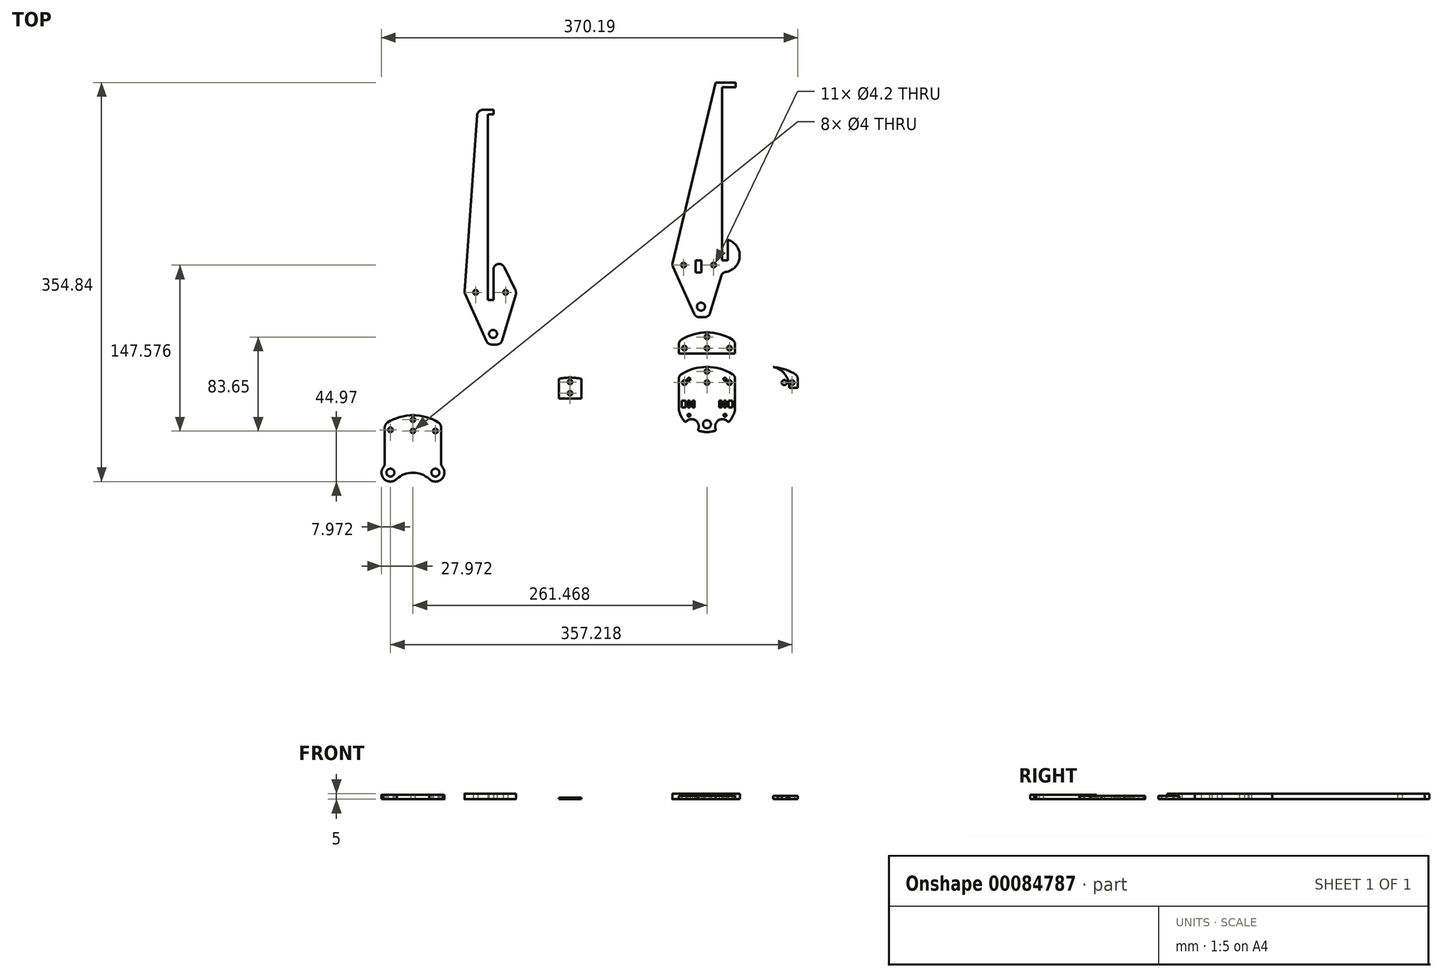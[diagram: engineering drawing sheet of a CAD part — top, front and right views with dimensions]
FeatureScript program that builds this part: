
annotation { "Feature Type Name" : "Feature", "Feature Type Description" : "" }
export const myFeature = defineFeature(function(context is Context, id is Id, definition is map)
    precondition{}
    {
        {
            var Q0;
            Q0=qCreatedBy(makeId("Top.planeOp"),FACE);
            var sketch = newSketch(context, id + "F0", { "sketchPlane" : qUnion([Q0])});
            skPoint(sketch, "E0.middle", {"position": v(0, 0) * mm});
            skLineSegment(sketch, "E1.top", {"start": v(-25, -10.03) * mm, "end": v(22.32, -10.03) * mm, "construction": true});
            skLineSegment(sketch, "E2.bottom", {"start": v(-20, 19) * mm, "end": v(20, 19) * mm, "construction": true});
            skCircle(sketch, "E3", {"center": v(-20, 19) * mm, "radius": 10 * mm, "construction": true});
            skCircle(sketch, "E4", {"center": v(0, -18) * mm, "radius": 10 * mm, "construction": true});
            skLineSegment(sketch, "E5.left", {"start": v(-25, 22.31) * mm, "end": v(-25, -5.6) * mm});
            skLineSegment(sketch, "E5.right", {"start": v(25, 22.31) * mm, "end": v(25, -5.6) * mm});
            skCircle(sketch, "E6", {"center": v(0, -18) * mm, "radius": 3.56 * mm});
            skCircle(sketch, "E7", {"center": v(-20, 19) * mm, "radius": 2.1 * mm});
            skCircle(sketch, "E8", {"center": v(20, 19) * mm, "radius": 2.1 * mm});
            skLineSegment(sketch, "E9", {"start": v(0, 0) * mm, "end": v(-25, 0) * mm, "construction": true});
            skLineSegment(sketch, "E10", {"start": v(0, 0) * mm, "end": v(0, 25) * mm, "construction": true});
            skLineSegment(sketch, "E11.bottom", {"start": v(-19, 3) * mm, "end": v(-22.5, 3) * mm});
            skLineSegment(sketch, "E11.top", {"start": v(-19, -3) * mm, "end": v(-22.5, -3) * mm});
            skLineSegment(sketch, "E11.left", {"start": v(-19, 3) * mm, "end": v(-19, -3) * mm});
            skLineSegment(sketch, "E11.right", {"start": v(-22.5, 3) * mm, "end": v(-22.5, -3) * mm});
            skPoint(sketch, "E11.middle", {"position": v(-20.75, 0) * mm});
            skLineSegment(sketch, "E12.bottom", {"start": v(-15, 3) * mm, "end": v(-17, 3) * mm});
            skLineSegment(sketch, "E12.top", {"start": v(-15, -3) * mm, "end": v(-17, -3) * mm});
            skLineSegment(sketch, "E12.left", {"start": v(-15, 3) * mm, "end": v(-15, -3) * mm});
            skLineSegment(sketch, "E12.right", {"start": v(-17, 3) * mm, "end": v(-17, -3) * mm});
            skPoint(sketch, "E12.middle", {"position": v(-16, 0) * mm});
            skLineSegment(sketch, "E13.bottom", {"start": v(-13, 3) * mm, "end": v(-11, 3) * mm});
            skLineSegment(sketch, "E13.top", {"start": v(-13, -3) * mm, "end": v(-11, -3) * mm});
            skLineSegment(sketch, "E13.left", {"start": v(-13, 3) * mm, "end": v(-13, -3) * mm});
            skLineSegment(sketch, "E13.right", {"start": v(-11, 3) * mm, "end": v(-11, -3) * mm});
            skPoint(sketch, "E13.middle", {"position": v(-12, 0) * mm});
            skLineSegment(sketch, "E14.MirrorCS", {"start": v(15, 3) * mm, "end": v(17, 3) * mm});
            skLineSegment(sketch, "E15.MirrorCS", {"start": v(13, -3) * mm, "end": v(11, -3) * mm});
            skLineSegment(sketch, "E16.MirrorCS", {"start": v(11, 3) * mm, "end": v(11, -3) * mm});
            skLineSegment(sketch, "E17.MirrorCS", {"start": v(13, 3) * mm, "end": v(11, 3) * mm});
            skPoint(sketch, "E18.MirrorP", {"position": v(16, 0) * mm});
            skLineSegment(sketch, "E19.MirrorCS", {"start": v(0, 0) * mm, "end": v(25, 0) * mm, "construction": true});
            skLineSegment(sketch, "E20.MirrorCS", {"start": v(22.5, 3) * mm, "end": v(22.5, -3) * mm});
            skLineSegment(sketch, "E21.MirrorCS", {"start": v(13, 3) * mm, "end": v(13, -3) * mm});
            skLineSegment(sketch, "E22.MirrorCS", {"start": v(15, 3) * mm, "end": v(15, -3) * mm});
            skLineSegment(sketch, "E23.MirrorCS", {"start": v(19, 3) * mm, "end": v(22.5, 3) * mm});
            skPoint(sketch, "E24.MirrorP", {"position": v(12, 0) * mm});
            skLineSegment(sketch, "E25.MirrorCS", {"start": v(19, 3) * mm, "end": v(19, -3) * mm});
            skLineSegment(sketch, "E26.MirrorCS", {"start": v(17, 3) * mm, "end": v(17, -3) * mm});
            skPoint(sketch, "E27.MirrorP", {"position": v(20.75, 0) * mm});
            skLineSegment(sketch, "E28.MirrorCS", {"start": v(19, -3) * mm, "end": v(22.5, -3) * mm});
            skLineSegment(sketch, "E29", {"start": v(15, -3) * mm, "end": v(17, -3) * mm});
            skCircle(sketch, "E30", {"center": v(0, 19) * mm, "radius": 2 * mm});
            skCircle(sketch, "E31", {"center": v(0, 29) * mm, "radius": 2 * mm});
            skLineSegment(sketch, "E32", {"start": v(0, 25) * mm, "end": v(0, 29) * mm, "construction": true});
            skArc(sketch, "E33", {"start": v(22.62, 26.57) * mm, "mid": v(0, 32.96) * mm, "end": v(-22.62, 26.57) * mm});
            skPoint(sketch, "E34", {"position": v(-20, 9) * mm});
            skPoint(sketch, "E35", {"position": v(-20, 10) * mm});
            skPoint(sketch, "E36.visualSharp", {"position": v(-25, -10.03) * mm});
            skPoint(sketch, "E37.visualSharp", {"position": v(-8, -24) * mm});
            skPoint(sketch, "E38", {"position": v(0, -8) * mm});
            skPoint(sketch, "E39", {"position": v(0, -10) * mm});
            skPoint(sketch, "E40.visualSharp", {"position": v(-25, 25) * mm});
            skArc(sketch, "E40.filletArc", {"start": v(-22.62, 26.57) * mm, "mid": v(-24.36, 24.75) * mm, "end": v(-25, 22.31) * mm});
            skPoint(sketch, "E41.visualSharp", {"position": v(25, 25) * mm});
            skArc(sketch, "E41.filletArc", {"start": v(25, 22.31) * mm, "mid": v(24.36, 24.75) * mm, "end": v(22.62, 26.57) * mm});
            skLineSegment(sketch, "E42.bottom", {"start": v(16, 22) * mm, "end": v(-16, 22) * mm, "construction": true});
            skLineSegment(sketch, "E42.top", {"start": v(16, -10) * mm, "end": v(-16, -10) * mm, "construction": true});
            skLineSegment(sketch, "E42.left", {"start": v(16, 22) * mm, "end": v(16, -10) * mm, "construction": true});
            skLineSegment(sketch, "E42.right", {"start": v(-16, 22) * mm, "end": v(-16, -10) * mm, "construction": true});
            skPoint(sketch, "E42.middle", {"position": v(0, 6) * mm});
            skCircle(sketch, "E43", {"center": v(-16, -10) * mm, "radius": 1.25 * mm});
            skCircle(sketch, "E44", {"center": v(16, -10) * mm, "radius": 1.25 * mm});
            skCircle(sketch, "E45", {"center": v(16, 22) * mm, "radius": 1.25 * mm});
            skCircle(sketch, "E46", {"center": v(-16, 22) * mm, "radius": 1.25 * mm});
            skPoint(sketch, "E47.orphan", {"position": v(25, -10.03) * mm});
            skPoint(sketch, "E48.orphan", {"position": v(8, -24) * mm});
            skLineSegment(sketch, "E49", {"start": v(-25, 14.31) * mm, "end": v(25, 14.31) * mm});
            skPoint(sketch, "E50.visualSharp", {"position": v(-21.13, -10.47) * mm});
            skArc(sketch, "E51", {"start": v(-25, -5.6) * mm, "mid": v(-23.01, -10.83) * mm, "end": v(-19.94, -15.51) * mm});
            skLineSegment(sketch, "E52", {"start": v(0, -18) * mm, "end": v(0, -24.93) * mm, "construction": true});
            skArc(sketch, "E53", {"start": v(0, -24.93) * mm, "mid": v(3.6, -24.67) * mm, "end": v(7.14, -23.92) * mm});
            skArc(sketch, "E54", {"start": v(-7.79, -22.56) * mm, "mid": v(-10.18, -14.59) * mm, "end": v(-18.44, -15.56) * mm});
            skArc(sketch, "E55.MirrorCS", {"start": v(7.79, -22.56) * mm, "mid": v(10.18, -14.59) * mm, "end": v(18.44, -15.56) * mm});
            skArc(sketch, "E56.trimOffspring", {"start": v(-7.14, -23.92) * mm, "mid": v(-3.6, -24.67) * mm, "end": v(0, -24.93) * mm});
            skArc(sketch, "E57.trimOffspring", {"start": v(19.94, -15.51) * mm, "mid": v(23.01, -10.83) * mm, "end": v(25, -5.6) * mm});
            skPoint(sketch, "E58.visualSharp", {"position": v(-19.14, -16.44) * mm});
            skArc(sketch, "E58.filletArc", {"start": v(-19.94, -15.51) * mm, "mid": v(-19.2, -15.88) * mm, "end": v(-18.44, -15.56) * mm});
            skPoint(sketch, "E59.visualSharp", {"position": v(-8.32, -23.55) * mm});
            skArc(sketch, "E59.filletArc", {"start": v(-7.79, -22.56) * mm, "mid": v(-7.77, -23.38) * mm, "end": v(-7.14, -23.92) * mm});
            skPoint(sketch, "E60.visualSharp", {"position": v(8.32, -23.55) * mm});
            skArc(sketch, "E60.filletArc", {"start": v(7.14, -23.92) * mm, "mid": v(7.77, -23.38) * mm, "end": v(7.79, -22.56) * mm});
            skPoint(sketch, "E61.visualSharp", {"position": v(19.14, -16.44) * mm});
            skArc(sketch, "E61.filletArc", {"start": v(18.44, -15.56) * mm, "mid": v(19.2, -15.88) * mm, "end": v(19.94, -15.51) * mm});
            skCircle(sketch, "E62", {"center": v(-121.74, 9.5) * mm, "radius": 2 * mm});
            skCircle(sketch, "E63", {"center": v(-121.76, 19.5) * mm, "radius": 2 * mm});
            skLineSegment(sketch, "E64", {"start": v(-121.76, 15.5) * mm, "end": v(-121.76, 19.5) * mm, "construction": true});
            skArc(sketch, "E65", {"start": v(-111.76, 22.3) * mm, "mid": v(-121.76, 23.47) * mm, "end": v(-131.76, 22.3) * mm});
            skLineSegment(sketch, "E66", {"start": v(-131.76, 4.82) * mm, "end": v(-111.76, 4.82) * mm});
            skLineSegment(sketch, "E67.left", {"start": v(-111.76, 22.3) * mm, "end": v(-111.76, 4.82) * mm});
            skLineSegment(sketch, "E67.right", {"start": v(-131.76, 22.3) * mm, "end": v(-131.76, 4.82) * mm});
            skPoint(sketch, "E67.middle", {"position": v(-121.76, 15.5) * mm});
            skCircle(sketch, "E68", {"center": v(-205.7, 99.28) * mm, "radius": 10 * mm, "construction": true});
            skCircle(sketch, "E69", {"center": v(-205.7, 99.28) * mm, "radius": 2.1 * mm});
            skPoint(sketch, "E70", {"position": v(-210.97, 90.79) * mm});
            skPoint(sketch, "E71", {"position": v(-211.85, 92.36) * mm});
            skCircle(sketch, "E72.MirrorC", {"center": v(-179.02, 99.28) * mm, "radius": 2.1 * mm});
            skLineSegment(sketch, "E73.bottom", {"start": v(-194.86, 103.37) * mm, "end": v(-189.86, 103.37) * mm});
            skLineSegment(sketch, "E73.top", {"start": v(-194.86, 92.57) * mm, "end": v(-189.86, 92.57) * mm});
            skLineSegment(sketch, "E73.left", {"start": v(-194.86, 103.37) * mm, "end": v(-194.86, 92.57) * mm});
            skLineSegment(sketch, "E73.right", {"start": v(-189.86, 103.37) * mm, "end": v(-189.86, 92.57) * mm});
            skPoint(sketch, "E73.middle", {"position": v(-192.36, 97.97) * mm});
            skCircle(sketch, "E74", {"center": v(-190.23, 62.28) * mm, "radius": 3.6 * mm});
            skLineSegment(sketch, "E75", {"start": v(-194.86, 103.37) * mm, "end": v(-194.86, 257.57) * mm});
            skLineSegment(sketch, "E76", {"start": v(-194.86, 261.57) * mm, "end": v(-199.34, 261.57) * mm});
            skLineSegment(sketch, "E77", {"start": v(-204.33, 256.93) * mm, "end": v(-215.6, 100.54) * mm});
            skLineSegment(sketch, "E78", {"start": v(-215.18, 98.13) * mm, "end": v(-196.18, 55.83) * mm});
            skLineSegment(sketch, "E79", {"start": v(-191.62, 52.88) * mm, "end": v(-190.23, 52.88) * mm});
            skLineSegment(sketch, "E80", {"start": v(-189.86, 103.37) * mm, "end": v(-189.86, 119.56) * mm});
            skLineSegment(sketch, "E81", {"start": v(-180.37, 121.76) * mm, "end": v(-170.39, 101.4) * mm});
            skLineSegment(sketch, "E82", {"start": v(-170.03, 97.03) * mm, "end": v(-182.22, 56.44) * mm});
            skLineSegment(sketch, "E83", {"start": v(-187.01, 52.88) * mm, "end": v(-190.23, 52.88) * mm});
            skPoint(sketch, "E84.visualSharp", {"position": v(-189.86, 141.11) * mm});
            skArc(sketch, "E84.filletArc", {"start": v(-180.37, 121.76) * mm, "mid": v(-185.99, 124.43) * mm, "end": v(-189.86, 119.56) * mm});
            skPoint(sketch, "E85.visualSharp", {"position": v(-204, 261.57) * mm});
            skArc(sketch, "E85.filletArc", {"start": v(-199.34, 261.57) * mm, "mid": v(-202.75, 260.23) * mm, "end": v(-204.33, 256.93) * mm});
            skPoint(sketch, "E86.visualSharp", {"position": v(-215.7, 99.28) * mm});
            skArc(sketch, "E86.filletArc", {"start": v(-215.6, 100.54) * mm, "mid": v(-215.54, 99.3) * mm, "end": v(-215.18, 98.13) * mm});
            skPoint(sketch, "E87.visualSharp", {"position": v(-194.86, 52.88) * mm});
            skArc(sketch, "E87.filletArc", {"start": v(-196.18, 55.83) * mm, "mid": v(-194.34, 53.68) * mm, "end": v(-191.62, 52.88) * mm});
            skPoint(sketch, "E88.visualSharp", {"position": v(-183.3, 52.88) * mm});
            skArc(sketch, "E88.filletArc", {"start": v(-187.01, 52.88) * mm, "mid": v(-184.03, 53.87) * mm, "end": v(-182.22, 56.44) * mm});
            skPoint(sketch, "E89.visualSharp", {"position": v(-169.35, 99.28) * mm});
            skArc(sketch, "E89.filletArc", {"start": v(-170.03, 97.03) * mm, "mid": v(-169.8, 99.24) * mm, "end": v(-170.39, 101.4) * mm});
            skLineSegment(sketch, "E90.bottom", {"start": v(-194.86, 261.57) * mm, "end": v(-189.86, 261.57) * mm});
            skLineSegment(sketch, "E90.top", {"start": v(-194.86, 257.57) * mm, "end": v(-189.86, 257.57) * mm});
            skLineSegment(sketch, "E90.right", {"start": v(-189.86, 261.57) * mm, "end": v(-189.86, 257.57) * mm});
            skCircle(sketch, "E91", {"center": v(-20.78, 123.53) * mm, "radius": 10 * mm, "construction": true});
            skCircle(sketch, "E92", {"center": v(-20.78, 123.53) * mm, "radius": 2.1 * mm});
            skPoint(sketch, "E93", {"position": v(-26.06, 115.03) * mm});
            skPoint(sketch, "E94", {"position": v(-26.94, 116.6) * mm});
            skCircle(sketch, "E95.MirrorC", {"center": v(5.89, 123.53) * mm, "radius": 2.1 * mm});
            skLineSegment(sketch, "E96.bottom", {"start": v(-9.95, 127.61) * mm, "end": v(-4.95, 127.61) * mm});
            skLineSegment(sketch, "E96.top", {"start": v(-9.95, 116.82) * mm, "end": v(-4.95, 116.82) * mm});
            skLineSegment(sketch, "E96.left", {"start": v(-9.95, 127.61) * mm, "end": v(-9.95, 116.82) * mm});
            skLineSegment(sketch, "E96.right", {"start": v(-4.95, 127.61) * mm, "end": v(-4.95, 116.82) * mm});
            skPoint(sketch, "E96.middle", {"position": v(-7.45, 122.22) * mm});
            skCircle(sketch, "E97", {"center": v(-5.31, 86.53) * mm, "radius": 3.6 * mm});
            skLineSegment(sketch, "E98", {"start": v(-9.95, 127.61) * mm, "end": v(-9.95, 281.82) * mm, "construction": true});
            skLineSegment(sketch, "E99", {"start": v(-9.95, 285.82) * mm, "end": v(-14.43, 285.82) * mm});
            skLineSegment(sketch, "E100", {"start": v(-19.42, 281.18) * mm, "end": v(-30.7, 124.78) * mm, "construction": true});
            skLineSegment(sketch, "E101", {"start": v(-30.26, 122.38) * mm, "end": v(-11.27, 80.08) * mm});
            skLineSegment(sketch, "E102", {"start": v(-6.71, 77.13) * mm, "end": v(-5.31, 77.13) * mm});
            skLineSegment(sketch, "E103", {"start": v(-4.95, 127.61) * mm, "end": v(-4.95, 143.8) * mm});
            skLineSegment(sketch, "E104", {"start": v(4.54, 146) * mm, "end": v(14.53, 125.64) * mm});
            skLineSegment(sketch, "E105", {"start": v(12.67, 113.9) * mm, "end": v(2.69, 80.69) * mm});
            skLineSegment(sketch, "E106", {"start": v(-2.1, 77.13) * mm, "end": v(-5.31, 77.13) * mm});
            skPoint(sketch, "E107.visualSharp", {"position": v(-4.95, 165.36) * mm});
            skArc(sketch, "E107.filletArc", {"start": v(4.54, 146) * mm, "mid": v(-1.08, 148.67) * mm, "end": v(-4.95, 143.8) * mm});
            skPoint(sketch, "E108.visualSharp", {"position": v(-19.08, 285.82) * mm});
            skArc(sketch, "E108.filletArc", {"start": v(-14.43, 285.82) * mm, "mid": v(-17.84, 284.48) * mm, "end": v(-19.42, 281.18) * mm});
            skPoint(sketch, "E109.visualSharp", {"position": v(-30.78, 123.53) * mm});
            skArc(sketch, "E109.filletArc", {"start": v(-30.7, 124.78) * mm, "mid": v(-30.63, 123.55) * mm, "end": v(-30.26, 122.38) * mm});
            skPoint(sketch, "E110.visualSharp", {"position": v(-9.95, 77.13) * mm});
            skArc(sketch, "E110.filletArc", {"start": v(-11.27, 80.08) * mm, "mid": v(-9.43, 77.93) * mm, "end": v(-6.71, 77.13) * mm});
            skPoint(sketch, "E111.visualSharp", {"position": v(1.62, 77.13) * mm});
            skArc(sketch, "E111.filletArc", {"start": v(-2.1, 77.13) * mm, "mid": v(0.88, 78.11) * mm, "end": v(2.69, 80.69) * mm});
            skPoint(sketch, "E112.visualSharp", {"position": v(15.56, 123.53) * mm});
            skArc(sketch, "E112.filletArc", {"start": v(14.88, 121.27) * mm, "mid": v(15.12, 123.49) * mm, "end": v(14.53, 125.64) * mm, "construction": true});
            skLineSegment(sketch, "E113.bottom", {"start": v(-9.95, 285.82) * mm, "end": v(-4.95, 285.82) * mm});
            skLineSegment(sketch, "E113.top", {"start": v(-9.95, 281.82) * mm, "end": v(-4.95, 281.82) * mm});
            skLineSegment(sketch, "E113.right", {"start": v(-4.95, 285.82) * mm, "end": v(-4.95, 281.82) * mm});
            skLineSegment(sketch, "E114", {"start": v(13.56, 127.61) * mm, "end": v(18.56, 127.61) * mm});
            skLineSegment(sketch, "E115", {"start": v(18.56, 127.61) * mm, "end": v(18.56, 146) * mm});
            skLineSegment(sketch, "E116", {"start": v(13.56, 127.61) * mm, "end": v(13.56, 281.82) * mm});
            skLineSegment(sketch, "E117", {"start": v(13.56, 285.82) * mm, "end": v(25.62, 285.82) * mm});
            skLineSegment(sketch, "E118", {"start": v(25.62, 285.82) * mm, "end": v(25.62, 281.82) * mm});
            skLineSegment(sketch, "E119", {"start": v(25.62, 281.82) * mm, "end": v(13.56, 281.82) * mm});
            skLineSegment(sketch, "E120", {"start": v(7.98, 281.82) * mm, "end": v(7.8, 285.82) * mm});
            skLineSegment(sketch, "E121", {"start": v(7.8, 285.82) * mm, "end": v(-30.7, 124.78) * mm});
            skLineSegment(sketch, "E122", {"start": v(7.8, 285.82) * mm, "end": v(13.56, 285.82) * mm});
            skCircle(sketch, "E123", {"center": v(5.89, 123.53) * mm, "radius": 10 * mm, "construction": true});
            skArc(sketch, "E124", {"start": v(16.7, 117.4) * mm, "mid": v(29.12, 130.96) * mm, "end": v(18.56, 146) * mm});
            skArc(sketch, "E125.filletArc", {"start": v(16.7, 117.4) * mm, "mid": v(14.18, 116.24) * mm, "end": v(12.67, 113.9) * mm});
            skCircle(sketch, "E126", {"center": v(-281.47, -23.05) * mm, "radius": 10 * mm, "construction": true});
            skLineSegment(sketch, "E127.right", {"start": v(-236.47, -20.74) * mm, "end": v(-236.47, -26.43) * mm});
            skCircle(sketch, "E128", {"center": v(-281.47, -23.05) * mm, "radius": 2.1 * mm});
            skCircle(sketch, "E129", {"center": v(-241.47, -24.05) * mm, "radius": 2.1 * mm});
            skLineSegment(sketch, "E130", {"start": v(-261.47, -43.05) * mm, "end": v(-261.47, -18.05) * mm, "construction": true});
            skCircle(sketch, "E131", {"center": v(-261.47, -24.05) * mm, "radius": 2 * mm});
            skCircle(sketch, "E132", {"center": v(-261.47, -14.05) * mm, "radius": 2 * mm});
            skLineSegment(sketch, "E133", {"start": v(-261.47, -18.05) * mm, "end": v(-261.47, -14.05) * mm, "construction": true});
            skArc(sketch, "E134", {"start": v(-238.85, -16.48) * mm, "mid": v(-261.47, -10.09) * mm, "end": v(-284.08, -16.48) * mm});
            skPoint(sketch, "E135", {"position": v(-281.47, -33.05) * mm});
            skPoint(sketch, "E136.visualSharp", {"position": v(-286.47, -53.08) * mm});
            skPoint(sketch, "E137.visualSharp", {"position": v(-269.47, -67.05) * mm});
            skPoint(sketch, "E138", {"position": v(-261.47, -51.05) * mm});
            skPoint(sketch, "E139", {"position": v(-261.47, -53.05) * mm});
            skPoint(sketch, "E140.visualSharp", {"position": v(-286.47, -18.05) * mm});
            skArc(sketch, "E140.filletArc", {"start": v(-284.08, -16.48) * mm, "mid": v(-285.83, -18.3) * mm, "end": v(-286.47, -20.74) * mm});
            skPoint(sketch, "E141.visualSharp", {"position": v(-236.47, -18.05) * mm});
            skArc(sketch, "E141.filletArc", {"start": v(-236.47, -20.74) * mm, "mid": v(-237.1, -18.3) * mm, "end": v(-238.85, -16.48) * mm});
            skLineSegment(sketch, "E142.left", {"start": v(-245.47, -21.05) * mm, "end": v(-245.47, -53.05) * mm, "construction": true});
            skPoint(sketch, "E143.orphan", {"position": v(-236.47, -53.08) * mm});
            skPoint(sketch, "E144.orphan", {"position": v(-253.46, -67.05) * mm});
            skPoint(sketch, "E145.visualSharp", {"position": v(-282.6, -53.52) * mm});
            skLineSegment(sketch, "E146", {"start": v(-261.47, -61.05) * mm, "end": v(-261.47, -67.98) * mm, "construction": true});
            skPoint(sketch, "E147.visualSharp", {"position": v(-280.6, -59.5) * mm});
            skPoint(sketch, "E148.visualSharp", {"position": v(-269.79, -66.6) * mm});
            skPoint(sketch, "E149.visualSharp", {"position": v(-253.15, -66.6) * mm});
            skPoint(sketch, "E150.visualSharp", {"position": v(-242.33, -59.5) * mm});
            skLineSegment(sketch, "E151", {"start": v(-241.47, -61.05) * mm, "end": v(-261.47, -61.05) * mm, "construction": true});
            skLineSegment(sketch, "E152", {"start": v(-241.47, -24.05) * mm, "end": v(-241.47, -61.05) * mm, "construction": true});
            skPoint(sketch, "E153.orphan", {"position": v(-230.17, -61.05) * mm});
            skCircle(sketch, "E154", {"center": v(-241.47, -61.05) * mm, "radius": 3.56 * mm});
            skCircle(sketch, "E155.MirrorC", {"center": v(-281.47, -61.05) * mm, "radius": 3.56 * mm});
            skLineSegment(sketch, "E156.MirrorCS", {"start": v(-281.47, -24.05) * mm, "end": v(-281.47, -61.05) * mm, "construction": true});
            skLineSegment(sketch, "E157.MirrorCS", {"start": v(-286.47, -20.74) * mm, "end": v(-286.47, -26.43) * mm});
            skCircle(sketch, "E158", {"center": v(-281.47, -61.05) * mm, "radius": 11 * mm, "construction": true});
            skPoint(sketch, "E159", {"position": v(-281.47, -50.05) * mm});
            skArc(sketch, "E160", {"start": v(-287.61, -55.98) * mm, "mid": v(-285.33, -68.02) * mm, "end": v(-273.9, -63.57) * mm});
            skArc(sketch, "E161", {"start": v(-286.47, -54.84) * mm, "mid": v(-285.26, -53) * mm, "end": v(-285.17, -50.81) * mm});
            skArc(sketch, "E162.MirrorC", {"start": v(-235.32, -55.98) * mm, "mid": v(-237.6, -68.02) * mm, "end": v(-249.03, -63.57) * mm});
            skArc(sketch, "E163.MirrorCS", {"start": v(-236.47, -54.84) * mm, "mid": v(-237.68, -53) * mm, "end": v(-237.77, -50.81) * mm});
            skPoint(sketch, "E164.visualSharp", {"position": v(-261.47, -63.49) * mm});
            skArc(sketch, "E164.filletArc", {"start": v(-264.14, -60.15) * mm, "mid": v(-261.47, -60.93) * mm, "end": v(-258.8, -60.15) * mm});
            skArc(sketch, "E165", {"start": v(-284.16, -46.5) * mm, "mid": v(-281.37, -38.08) * mm, "end": v(-284.99, -29.99) * mm});
            skPoint(sketch, "E166.orphan", {"position": v(-286.47, -48.65) * mm});
            skArc(sketch, "E167.filletArc", {"start": v(-284.16, -46.5) * mm, "mid": v(-285.17, -48.53) * mm, "end": v(-285.17, -50.81) * mm});
            skPoint(sketch, "E168.visualSharp", {"position": v(-286.47, -28.74) * mm});
            skArc(sketch, "E168.filletArc", {"start": v(-286.47, -26.43) * mm, "mid": v(-286.08, -28.36) * mm, "end": v(-284.99, -29.99) * mm});
            skArc(sketch, "E169.MirrorCS", {"start": v(-236.47, -26.43) * mm, "mid": v(-236.85, -28.36) * mm, "end": v(-237.95, -29.99) * mm});
            skArc(sketch, "E170.MirrorCS", {"start": v(-238.78, -46.5) * mm, "mid": v(-241.57, -38.08) * mm, "end": v(-237.95, -29.99) * mm});
            skArc(sketch, "E171.MirrorCS", {"start": v(-238.78, -46.5) * mm, "mid": v(-237.77, -48.53) * mm, "end": v(-237.77, -50.81) * mm});
            skPoint(sketch, "E172.orphan", {"position": v(-236.47, -48.65) * mm});
            skArc(sketch, "E173", {"start": v(-237.95, -29.99) * mm, "mid": v(-243.47, -42.79) * mm, "end": v(-236.47, -54.84) * mm});
            skArc(sketch, "E174.MirrorCS", {"start": v(-284.99, -29.99) * mm, "mid": v(-279.47, -42.79) * mm, "end": v(-286.47, -54.84) * mm});
            skLineSegment(sketch, "E175", {"start": v(-247.05, -66.73) * mm, "end": v(-258.06, -56.48) * mm});
            skLineSegment(sketch, "E176.MirrorCS", {"start": v(-275.88, -66.73) * mm, "end": v(-264.88, -56.48) * mm});
            skArc(sketch, "E177.filletArc", {"start": v(-258.06, -56.48) * mm, "mid": v(-261.47, -55.14) * mm, "end": v(-264.88, -56.48) * mm, "construction": true});
            skArc(sketch, "E178", {"start": v(-247.05, -66.73) * mm, "mid": v(-261.47, -61.06) * mm, "end": v(-275.88, -66.73) * mm});
            skLineSegment(sketch, "E179", {"start": v(-286.47, -26.43) * mm, "end": v(-286.47, -52.8) * mm});
            skLineSegment(sketch, "E180.MirrorCS", {"start": v(-236.47, -26.43) * mm, "end": v(-236.47, -52.8) * mm});
            skPoint(sketch, "E181.newPointA", {"position": v(-236.47, -57.06) * mm});
            skArc(sketch, "E181.filletArc", {"start": v(-236.47, -52.8) * mm, "mid": v(-236.17, -54.48) * mm, "end": v(-235.32, -55.98) * mm});
            skPoint(sketch, "E182.newPointA", {"position": v(-286.47, -57.06) * mm});
            skArc(sketch, "E182.filletArc", {"start": v(-287.61, -55.98) * mm, "mid": v(-286.76, -54.48) * mm, "end": v(-286.47, -52.8) * mm});
            skArc(sketch, "E183", {"start": v(-285.83, -18.3) * mm, "mid": v(-293.27, -41.44) * mm, "end": v(-288.25, -65.23) * mm});
            skArc(sketch, "E184.MirrorCS", {"start": v(-237.1, -18.3) * mm, "mid": v(-229.66, -41.44) * mm, "end": v(-234.68, -65.23) * mm});
            skSolve(sketch);
        }
        {
            var Q0;
            Q0=makeQuery(id+"F0.imprint","IMPRINT",FACE,{"disambiguationData":[TD([[makeQuery(id+"F0.imprint","IMPRINT",EDGE,{"derivedFrom":sQuery(id+"F0.wireOp",EDGE,"E6")}),-1.0]])]});
            var Q1;
            Q1=makeQuery(id+"F0.imprint","IMPRINT",FACE,{"disambiguationData":[TD([[makeQuery(id+"F0.imprint","IMPRINT",EDGE,{"derivedFrom":sQuery(id+"F0.wireOp",EDGE,"E7")}),-1.0]])]});
            var Q2;
            Q2=makeQuery(id+"F0.imprint","IMPRINT",FACE,{"disambiguationData":[TD([[makeQuery(id+"F0.imprint","IMPRINT",EDGE,{"derivedFrom":sQuery(id+"F0.wireOp",EDGE,"AnCcxth8-TEnw-8CJA-Q1e5-bC0U5bzkQu75")}),1.0]])]});
            var Q3;
            {var subQ3=sQuery(id+"F0.wireOp",EDGE,"c200fd2f-bd05-45dd-b6f9-3ae92d8b672b0.MirrorCS");Q3=makeQuery(id+"F0.imprint","IMPRINT",FACE,{"disambiguationData":[TD([[makeQuery(id+"F0.imprint","IMPRINT",EDGE,{"derivedFrom":subQ3}),-1.0]])]});}
            var Q4;
            {var subQ0=sQuery(id+"F0.wireOp",EDGE,"69943f32-f5be-4bb6-8905-9935c4f36ada.filletArc");Q4=makeQuery(id+"F0.imprint","IMPRINT",FACE,{"disambiguationData":[TD([[makeQuery(id+"F0.imprint","IMPRINT",EDGE,{"derivedFrom":subQ0}),1.0]])]});}
            var Q5;
            {var subQ1=sQuery(id+"F0.wireOp",EDGE,"1c1e505f-d3b0-43af-af64-12dd094d3fbb0.MirrorCS");var subQ3=sQuery(id+"F0.wireOp",EDGE,"ab5f363a-6a9b-4e83-99b5-ab17280f4d850.MirrorCS");var subQ4=makeQuery(id+"F0.imprint","INTERSECT",VERTEX,{"disambiguationData":[OD(0.0)],"derivedFrom":[subQ1,subQ3]});Q5=makeQuery(id+"F0.imprint","IMPRINT",FACE,{"disambiguationData":[TD([[makeQuery(id+"F0.imprint","IMPRINT",EDGE,{"disambiguationData":[TD([[subQ4,-1.0]])],"derivedFrom":subQ3}),-1.0]])]});}
            extrude(context, id + "F1", {"entities" : qUnion([Q0, Q1, Q2, Q3, Q4, Q5]), "depth" : 3 * mm});
        }
        {
            var Q0;
            Q0=makeQuery(id+"F0.imprint","IMPRINT",FACE,{"disambiguationData":[TD([[makeQuery(id+"F0.imprint","IMPRINT",EDGE,{"derivedFrom":sQuery(id+"F0.wireOp",EDGE,"E7")}),-1.0]])]});
            var Q1;
            Q1=makeQuery(id+"F0.imprint","IMPRINT",FACE,{"disambiguationData":[TD([[makeQuery(id+"F0.imprint","IMPRINT",EDGE,{"derivedFrom":sQuery(id+"F0.wireOp",EDGE,"E46")}),1.0]])]});
            var Q2;
            Q2=makeQuery(id+"F0.imprint","IMPRINT",FACE,{"disambiguationData":[TD([[makeQuery(id+"F0.imprint","IMPRINT",EDGE,{"derivedFrom":sQuery(id+"F0.wireOp",EDGE,"E45")}),1.0]])]});
            extrude(context, id + "F2", {"entities" : qUnion([Q0, Q1, Q2]), "depth" : 3 * mm});
        }
        {
            var Q0;
            Q0=makeQuery(id+"F2.opExtrude","SWEPT_BODY",BODY,{"disambiguationData":[OSD([sQuery(id+"F0.wireOp",EDGE,"E5.left"),sQuery(id+"F0.wireOp",EDGE,"E5.right"),sQuery(id+"F0.wireOp",EDGE,"E7"),sQuery(id+"F0.wireOp",EDGE,"E8"),sQuery(id+"F0.wireOp",EDGE,"E30"),sQuery(id+"F0.wireOp",EDGE,"E31"),sQuery(id+"F0.wireOp",EDGE,"E33"),sQuery(id+"F0.wireOp",EDGE,"E40.filletArc"),sQuery(id+"F0.wireOp",EDGE,"E41.filletArc"),sQuery(id+"F0.wireOp",EDGE,"E45"),sQuery(id+"F0.wireOp",EDGE,"E46"),sQuery(id+"F0.wireOp",EDGE,"E49")])]});
            transform(context, id + "F3", {"entities" : qUnion([Q0]), "transformType" : TransformType.TRANSLATION_3D, "dx" : 55.75 * mm, "dy" : 0 * mm, "dz" : 0 * mm, "makeCopy" : false});
        }
        {
            var Q0;
            Q0=makeQuery(id+"F2.opExtrude","CAP_FACE",FACE,{"disambiguationData":[OSD([sQuery(id+"F0.wireOp",EDGE,"E5.left"),sQuery(id+"F0.wireOp",EDGE,"E5.right"),sQuery(id+"F0.wireOp",EDGE,"E7"),sQuery(id+"F0.wireOp",EDGE,"E8"),sQuery(id+"F0.wireOp",EDGE,"E30"),sQuery(id+"F0.wireOp",EDGE,"E31"),sQuery(id+"F0.wireOp",EDGE,"E33"),sQuery(id+"F0.wireOp",EDGE,"E40.filletArc"),sQuery(id+"F0.wireOp",EDGE,"E41.filletArc"),sQuery(id+"F0.wireOp",EDGE,"E49")])],"isStart":false});
            var sketch = newSketch(context, id + "F4", { "sketchPlane" : qUnion([Q0])});
            skLineSegment(sketch, "E185", {"start": v(55.75, 14.31) * mm, "end": v(55.75, 19) * mm, "construction": true});
            skLineSegment(sketch, "E186", {"start": v(55.75, 19) * mm, "end": v(42.75, 19) * mm, "construction": true});
            skCircle(sketch, "E187", {"center": v(42.75, 19) * mm, "radius": 10 * mm, "construction": true});
            skCircle(sketch, "E188", {"center": v(42.75, 19) * mm, "radius": 2.25 * mm});
            skCircle(sketch, "E189.MirrorC", {"center": v(68.75, 19) * mm, "radius": 2.25 * mm});
            skArc(sketch, "E190.MirrorCS", {"start": v(62.92, 31.63) * mm, "mid": v(70.65, 24.5) * mm, "end": v(73.2, 14.3) * mm});
            skLineSegment(sketch, "E191", {"start": v(45.75, 13.74) * mm, "end": v(45.75, 25.76) * mm});
            skPoint(sketch, "E192.newPointB", {"position": v(38.3, 14.3) * mm});
            skArc(sketch, "E193", {"start": v(62.92, 31.63) * mm, "mid": v(54.9, 32.88) * mm, "end": v(47.49, 29.55) * mm});
            skPoint(sketch, "E194.visualSharp", {"position": v(45.75, 27.76) * mm});
            skArc(sketch, "E194.filletArc", {"start": v(47.49, 29.55) * mm, "mid": v(46.2, 27.84) * mm, "end": v(45.75, 25.76) * mm});
            skSolve(sketch);
        }
        {
            var Q0;
            {var subQ2=sQuery(id+"F4.wireOp",EDGE,"W537BFPO-2DYj-tqX4-z8I5-l5NQawsHajvo");Q0=makeQuery(id+"F4.imprint","IMPRINT",FACE,{"disambiguationData":[TD([[makeQuery(id+"F4.imprint","IMPRINT",EDGE,{"derivedFrom":subQ2}),-1.0]])]});}
            var Q1;
            Q1=makeQuery(id+"F4.imprint","IMPRINT",FACE,{"disambiguationData":[TD([[makeQuery(id+"F4.imprint","IMPRINT",EDGE,{"derivedFrom":sQuery(id+"F4.wireOp",EDGE,"E188")}),1.0]])]});
            var Q2;
            Q2=makeQuery(id+"F4.imprint","IMPRINT",FACE,{"disambiguationData":[TD([[makeQuery(id+"F4.imprint","IMPRINT",EDGE,{"derivedFrom":sQuery(id+"F4.wireOp",EDGE,"E189.MirrorC")}),-1.0]])]});
            var Q3;
            {var subQ3=sQuery(id+"F4.wireOp",EDGE,"E190.MirrorCS");Q3=makeQuery(id+"F4.imprint","IMPRINT",FACE,{"disambiguationData":[TD([[makeQuery(id+"F4.imprint","IMPRINT",EDGE,{"derivedFrom":subQ3}),1.0]])]});}
            var Q4;
            Q4=makeQuery(id+"F4.imprint","IMPRINT",FACE,{"disambiguationData":[TD([[makeQuery(id+"F4.imprint","IMPRINT",EDGE,{"derivedFrom":sQuery(id+"F4.wireOp",EDGE,"E188")}),-1.0]])]});
            extrude(context, id + "F5", {"entities" : qUnion([Q0, Q1, Q2, Q3, Q4]), "operationType" : NewBodyOperationType.REMOVE, "oppositeDirection" : true, "depth" : 25 * mm});
        }
        {
            var Q0;
            Q0=makeQuery(id+"F0.imprint","IMPRINT",FACE,{"disambiguationData":[TD([[makeQuery(id+"F0.imprint","IMPRINT",EDGE,{"derivedFrom":sQuery(id+"F0.wireOp",EDGE,"E7")}),-1.0]])]});
            var Q1;
            Q1=makeQuery(id+"F0.imprint","IMPRINT",FACE,{"disambiguationData":[TD([[makeQuery(id+"F0.imprint","IMPRINT",EDGE,{"derivedFrom":sQuery(id+"F0.wireOp",EDGE,"E45")}),1.0]])]});
            var Q2;
            Q2=makeQuery(id+"F0.imprint","IMPRINT",FACE,{"disambiguationData":[TD([[makeQuery(id+"F0.imprint","IMPRINT",EDGE,{"derivedFrom":sQuery(id+"F0.wireOp",EDGE,"E46")}),1.0]])]});
            extrude(context, id + "F6", {"entities" : qUnion([Q0, Q1, Q2]), "depth" : 3 * mm});
        }
        {
            var Q0;
            Q0=makeQuery(id+"F6.opExtrude","SWEPT_BODY",BODY,{"disambiguationData":[OSD([sQuery(id+"F0.wireOp",EDGE,"E5.left"),sQuery(id+"F0.wireOp",EDGE,"E5.right"),sQuery(id+"F0.wireOp",EDGE,"E7"),sQuery(id+"F0.wireOp",EDGE,"E8"),sQuery(id+"F0.wireOp",EDGE,"E30"),sQuery(id+"F0.wireOp",EDGE,"E31"),sQuery(id+"F0.wireOp",EDGE,"E33"),sQuery(id+"F0.wireOp",EDGE,"E40.filletArc"),sQuery(id+"F0.wireOp",EDGE,"E41.filletArc"),sQuery(id+"F0.wireOp",EDGE,"E45"),sQuery(id+"F0.wireOp",EDGE,"E46"),sQuery(id+"F0.wireOp",EDGE,"E49")])]});
            transform(context, id + "F7", {"entities" : qUnion([Q0]), "transformType" : TransformType.TRANSLATION_3D, "dx" : 0 * mm, "dy" : 30.6 * mm, "dz" : 0 * mm, "makeCopy" : false});
        }
        {
            var Q0;
            Q0=makeQuery(id+"F0.imprint","IMPRINT",FACE,{"disambiguationData":[TD([[makeQuery(id+"F0.imprint","IMPRINT",EDGE,{"derivedFrom":sQuery(id+"F0.wireOp",EDGE,"E62")}),-1.0]])]});
            extrude(context, id + "F8", {"entities" : qUnion([Q0]), "depth" : 1.25 * mm});
        }
        {
            var Q0;
            Q0=makeQuery(id+"F0.imprint","IMPRINT",FACE,{"disambiguationData":[TD([[makeQuery(id+"F0.imprint","IMPRINT",EDGE,{"derivedFrom":sQuery(id+"F0.wireOp",EDGE,"E69")}),-1.0]])]});
            var Q1;
            Q1=makeQuery(id+"F0.imprint","IMPRINT",FACE,{"disambiguationData":[TD([[makeQuery(id+"F0.imprint","IMPRINT",EDGE,{"derivedFrom":sQuery(id+"F0.wireOp",EDGE,"E92")}),-1.0]])]});
            extrude(context, id + "F9", {"entities" : qUnion([Q0, Q1]), "depth" : 5 * mm});
        }
        {
            var Q0;
            Q0=makeQuery(id+"F0.imprint","IMPRINT",FACE,{"disambiguationData":[TD([[makeQuery(id+"F0.imprint","IMPRINT",EDGE,{"derivedFrom":sQuery(id+"F0.wireOp",EDGE,"E128")}),-1.0]])]});
            var Q1;
            Q1=makeQuery(id+"F0.imprint","IMPRINT",FACE,{"disambiguationData":[TD([[makeQuery(id+"F0.imprint","IMPRINT",EDGE,{"derivedFrom":sQuery(id+"F0.wireOp",EDGE,"E161")}),-1.0]])]});
            var Q2;
            {var subQ2=sQuery(id+"F0.wireOp",EDGE,"E161");Q2=makeQuery(id+"F0.imprint","IMPRINT",FACE,{"disambiguationData":[TD([[makeQuery(id+"F0.imprint","IMPRINT",EDGE,{"derivedFrom":subQ2}),1.0]])]});}
            var Q3;
            Q3=makeQuery(id+"F0.imprint","IMPRINT",FACE,{"disambiguationData":[TD([[makeQuery(id+"F0.imprint","IMPRINT",EDGE,{"derivedFrom":sQuery(id+"F0.wireOp",EDGE,"E163.MirrorCS")}),1.0]])]});
            var Q4;
            {var subQ2=sQuery(id+"F0.wireOp",EDGE,"E163.MirrorCS");Q4=makeQuery(id+"F0.imprint","IMPRINT",FACE,{"disambiguationData":[TD([[makeQuery(id+"F0.imprint","IMPRINT",EDGE,{"derivedFrom":subQ2}),-1.0]])]});}
            extrude(context, id + "F10", {"entities" : qUnion([Q0, Q1, Q2, Q3, Q4]), "depth" : 4 * mm});
        }
    });
